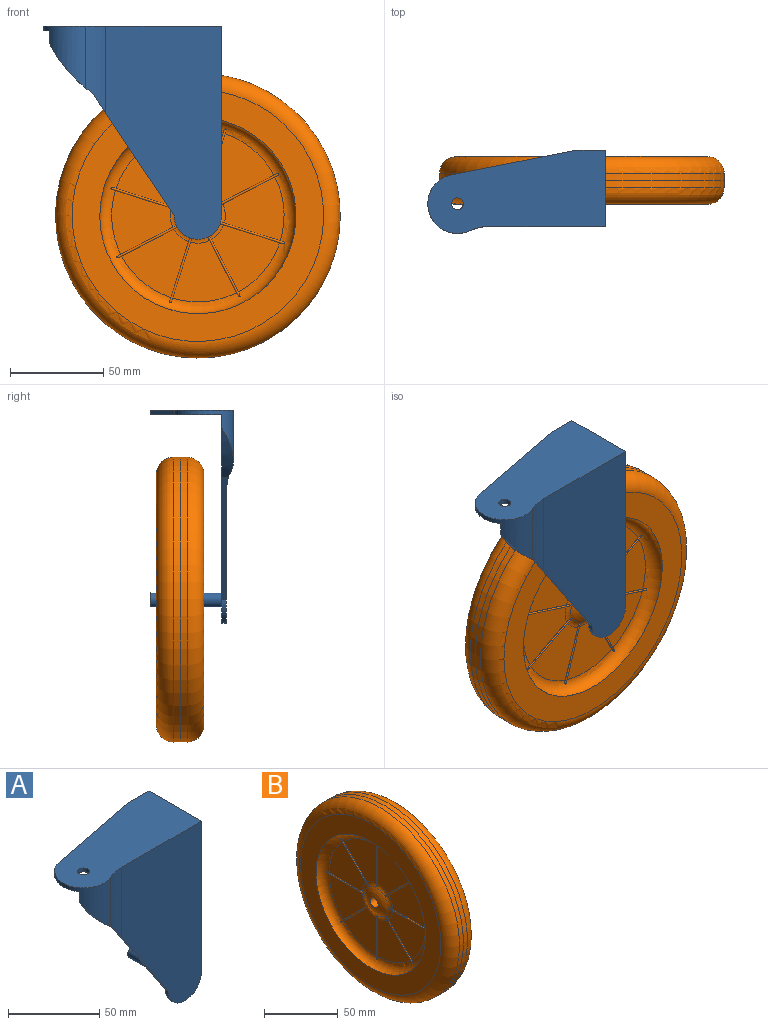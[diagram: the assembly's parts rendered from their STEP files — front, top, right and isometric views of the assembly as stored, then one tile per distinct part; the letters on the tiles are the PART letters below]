
ASSEMBLY  parts=2 mates=1
PART A: 15 faces, bbox 95.3x44.5x114.3 mm
  f0: cylinder r=15.88mm len=33.34mm, axis (0,0,1), area 566.9mm2, adj f2,f7,f9,f10,f12,f13
  f1: plane 65.49x43.66mm, normal (-0.83,0,-0.55), area 204mm2, adj f2,f5,f8,f9,f13
  f2: cylinder r=74.55mm len=26.54mm, axis (0,-1,0), area 164.4mm2, adj f0,f1,f9,f13
  f3: cylinder r=3.81mm len=38.1mm, axis (0,1,0), area 912.1mm2, adj f4,f9
  f4: plane 7.62x7.62mm, normal (0,1,0), area 45.6mm2, adj f3
  f5: cylinder r=12.7mm len=25.4mm, axis (0,1,0), area 101.3mm2, adj f1,f6,f8,f9
  f6: plane 101.6x40.64mm, normal (1,0,0), area 354.8mm2, adj f5,f7,f8,f9,f10,f11
  f7: plane 95.25x44.45mm, normal (0,0,1), area 3230.5mm2, adj f0,f6,f8,f11,f12,f13,f14
  f8: plane 114.3x62.05mm, normal (0,-1,0), area 5550.4mm2, adj f1,f5,f6,f7,f13
  f9: plane 111.76x92.08mm, normal (0,1,0), area 6135.8mm2, adj f0,f1,f2,f3,f5,f6,f10
  f10: plane 95.25x38.1mm, normal (0,0,-1), area 2942.1mm2, adj f0,f6,f9,f11,f12,f14
  f11: plane 16.51x2.54mm, normal (0,1,0), area 41.9mm2, adj f6,f7,f10,f12
  f12: plane 65.18x12.87mm, normal (-0.19,0.98,0), area 168.8mm2, adj f0,f7,f10,f11
  f13: cylinder r=25.4mm len=46.62mm, axis (0,0,1), area 428.8mm2, adj f0,f1,f2,f7,f8
  f14: cylinder r=3.17mm len=6.35mm, axis (0,0,1), area 50.7mm2, adj f7,f10
PART B: 79 faces, bbox 25.5x165.1x165.1 mm
  f0: plane 35.43x31.8mm, normal (1,0,0), area 720.9mm2, adj f8,f9,f25,f27
  f1: plane 35.43x31.8mm, normal (1,0,0), area 720.9mm2, adj f8,f9,f21,f24
  f2: plane 35.43x31.8mm, normal (1,0,0), area 720.9mm2, adj f8,f9,f28,f30
  f3: plane 35.43x31.8mm, normal (1,0,0), area 720.9mm2, adj f8,f9,f31,f33
  f4: plane 35.43x31.8mm, normal (1,0,0), area 720.9mm2, adj f8,f9,f34,f36
  f5: plane 35.43x31.8mm, normal (1,0,0), area 720.9mm2, adj f8,f9,f16,f37
  f6: plane 35.43x31.8mm, normal (1,0,0), area 720.9mm2, adj f8,f9,f15,f18
  f7: plane 35.43x31.8mm, normal (1,0,0), area 720.9mm2, adj f8,f9,f19,f22
  f8: torus R=46.2mm, axis (-1,0,0), area 3128.4mm2, adj f0,f1,f2,f3,f4,f5,f6,f7
  f9: torus R=14.73mm, axis (-1,0,0), area 273.1mm2, adj f0,f1,f2,f3,f4,f5,f6,f7
  f10: cone r=76.24mm half-angle=0deg, axis (1,0,0), area 1837mm2, adj f38,f77
  f11: plane 134.73x134.73mm, normal (1,0,0), area 5582.6mm2, adj f12,f77
  f12: cylinder r=52.55mm len=105.09mm, axis (-1,0,0), area 10.5mm2, adj f8,f11
  f13: torus R=3.81mm, axis (-1,0,0), area 382.2mm2, adj f9,f78
  f14: cylinder r=0.51mm len=26.76mm, axis (0,0.71,-0.71), area 57.2mm2, adj f8,f9,f15,f16
  f15: plane 23.72x23.72mm, normal (0,-0.71,-0.71), area 2.8mm2, adj f6,f8,f9,f14
  f16: plane 23.72x23.72mm, normal (0,0.71,0.71), area 2.8mm2, adj f5,f8,f9,f14
  f17: cylinder r=0.51mm len=36.82mm, axis (0,0,-1), area 57.2mm2, adj f8,f9,f18,f19
  f18: plane 33.54x0.09mm, normal (0,1,0), area 2.8mm2, adj f6,f8,f9,f17
  f19: plane 33.54x0.09mm, normal (0,-1,0), area 2.8mm2, adj f7,f8,f9,f17
  f20: cylinder r=0.51mm len=26.76mm, axis (0,-0.71,-0.71), area 57.2mm2, adj f8,f9,f21,f22
  f21: plane 23.72x23.72mm, normal (0,-0.71,0.71), area 2.8mm2, adj f1,f8,f9,f20
  f22: plane 23.72x23.72mm, normal (0,0.71,-0.71), area 2.8mm2, adj f7,f8,f9,f20
  f23: cylinder r=0.51mm len=36.82mm, axis (0,-1,0), area 57.2mm2, adj f8,f9,f24,f25
  f24: plane 33.54x0.09mm, normal (0,0,-1), area 2.8mm2, adj f1,f8,f9,f23
  f25: plane 33.54x0.09mm, normal (0,0,1), area 2.8mm2, adj f0,f8,f9,f23
  f26: cylinder r=0.51mm len=26.76mm, axis (0,-0.71,0.71), area 57.2mm2, adj f8,f9,f27,f28
  f27: plane 23.72x23.72mm, normal (0,-0.71,-0.71), area 2.8mm2, adj f0,f8,f9,f26
  f28: plane 23.72x23.72mm, normal (0,0.71,0.71), area 2.8mm2, adj f2,f8,f9,f26
  f29: cylinder r=0.51mm len=36.82mm, axis (0,0,1), area 57.2mm2, adj f8,f9,f30,f31
  f30: plane 33.54x0.09mm, normal (0,-1,0), area 2.8mm2, adj f2,f8,f9,f29
  f31: plane 33.54x0.09mm, normal (0,1,0), area 2.8mm2, adj f3,f8,f9,f29
  f32: cylinder r=0.51mm len=26.76mm, axis (0,0.71,0.71), area 57.2mm2, adj f8,f9,f33,f34
  f33: plane 23.72x23.72mm, normal (0,-0.71,0.71), area 2.8mm2, adj f3,f8,f9,f32
  f34: plane 23.72x23.72mm, normal (0,0.71,-0.71), area 2.8mm2, adj f4,f8,f9,f32
  f35: cylinder r=0.51mm len=36.82mm, axis (0,1,0), area 57.2mm2, adj f8,f9,f36,f37
  f36: plane 33.54x0.09mm, normal (0,0,1), area 2.8mm2, adj f4,f8,f9,f35
  f37: plane 33.54x0.09mm, normal (0,0,-1), area 2.8mm2, adj f5,f8,f9,f35
  f38: cone r=76.24mm half-angle=0deg, axis (-1,0,0), area 1837mm2, adj f10,f76
  f39: plane 134.73x134.73mm, normal (-1,0,0), area 5582.6mm2, adj f40,f76
  f40: cylinder r=52.55mm len=105.09mm, axis (-1,0,0), area 10.5mm2, adj f39,f42
  f41: torus R=14.73mm, axis (1,0,0), area 273mm2, adj f43,f44,f45,f46,f47,f48,f49,f50
  f42: torus R=46.2mm, axis (1,0,0), area 3128.9mm2, adj f40,f43,f44,f45,f46,f47,f48,f49
  f43: plane 35.43x31.8mm, normal (-1,0,0), area 720.9mm2, adj f41,f42,f55,f58
  f44: plane 35.43x31.8mm, normal (-1,0,0), area 720.9mm2, adj f41,f42,f53,f56
  f45: plane 35.43x31.8mm, normal (-1,0,0), area 720.9mm2, adj f41,f42,f52,f74
  f46: plane 35.43x31.8mm, normal (-1,0,0), area 720.9mm2, adj f41,f42,f71,f75
  f47: plane 35.43x31.8mm, normal (-1,0,0), area 720.9mm2, adj f41,f42,f68,f70
  f48: plane 35.43x31.8mm, normal (-1,0,0), area 720.9mm2, adj f41,f42,f65,f67
  f49: plane 35.43x31.8mm, normal (-1,0,0), area 720.9mm2, adj f41,f42,f62,f64
  f50: plane 35.43x31.8mm, normal (-1,0,0), area 720.9mm2, adj f41,f42,f59,f61
  f51: cylinder r=0.51mm len=36.82mm, axis (0,0,-1), area 57.2mm2, adj f41,f42,f52,f53
  f52: plane 33.54x0.09mm, normal (0,1,0), area 2.8mm2, adj f41,f42,f45,f51
  f53: plane 33.54x0.09mm, normal (0,-1,0), area 2.8mm2, adj f41,f42,f44,f51
  f54: cylinder r=0.51mm len=26.76mm, axis (0,-0.71,-0.71), area 57.2mm2, adj f41,f42,f55,f56
  f55: plane 23.72x23.72mm, normal (0,-0.71,0.71), area 2.8mm2, adj f41,f42,f43,f54
  f56: plane 23.72x23.72mm, normal (0,0.71,-0.71), area 2.8mm2, adj f41,f42,f44,f54
  f57: cylinder r=0.51mm len=36.82mm, axis (0,-1,0), area 57.2mm2, adj f41,f42,f58,f59
  f58: plane 33.54x0.09mm, normal (0,0,-1), area 2.8mm2, adj f41,f42,f43,f57
  f59: plane 33.54x0.09mm, normal (0,0,1), area 2.8mm2, adj f41,f42,f50,f57
  f60: cylinder r=0.51mm len=26.76mm, axis (0,-0.71,0.71), area 57.2mm2, adj f41,f42,f61,f62
  f61: plane 23.72x23.72mm, normal (0,-0.71,-0.71), area 2.8mm2, adj f41,f42,f50,f60
  f62: plane 23.72x23.72mm, normal (0,0.71,0.71), area 2.8mm2, adj f41,f42,f49,f60
  f63: cylinder r=0.51mm len=36.82mm, axis (0,0,1), area 57.2mm2, adj f41,f42,f64,f65
  f64: plane 33.54x0.09mm, normal (0,-1,0), area 2.8mm2, adj f41,f42,f49,f63
  f65: plane 33.54x0.09mm, normal (0,1,0), area 2.8mm2, adj f41,f42,f48,f63
  f66: cylinder r=0.51mm len=26.76mm, axis (0,0.71,0.71), area 57.2mm2, adj f41,f42,f67,f68
  f67: plane 23.72x23.72mm, normal (0,-0.71,0.71), area 2.8mm2, adj f41,f42,f48,f66
  f68: plane 23.72x23.72mm, normal (0,0.71,-0.71), area 2.8mm2, adj f41,f42,f47,f66
  f69: cylinder r=0.51mm len=36.82mm, axis (0,1,0), area 57.2mm2, adj f41,f42,f70,f71
  f70: plane 33.54x0.09mm, normal (0,0,1), area 2.8mm2, adj f41,f42,f47,f69
  f71: plane 33.54x0.09mm, normal (0,0,-1), area 2.8mm2, adj f41,f42,f46,f69
  f72: torus R=3.81mm, axis (-1,0,0), area 382.2mm2, adj f41,f78
  f73: cylinder r=0.51mm len=26.76mm, axis (0,0.71,-0.71), area 57.2mm2, adj f41,f42,f74,f75
  f74: plane 23.72x23.72mm, normal (0,-0.71,-0.71), area 2.8mm2, adj f41,f42,f45,f73
  f75: plane 23.72x23.72mm, normal (0,0.71,0.71), area 2.8mm2, adj f41,f42,f46,f73
  f76: torus R=67.37mm, axis (-1,0,0), area 6410.4mm2, adj f38,f39
  f77: torus R=67.37mm, axis (-1,0,0), area 6410.4mm2, adj f10,f11
  f78: cylinder r=3.81mm len=19.05mm, axis (1,0,0), area 456mm2, adj f13,f72
PLACE A t=(16.13,22.26,-25.57)mm fixed
PLACE B rot(axis=(-0.65,-0.65,0.4),136.8deg) t=(16.13,6.38,-25.57)mm
MATE revolute B.f78 <-> A.f3  axis (0,1,0) through (16.13,15.91,-25.57)mm
